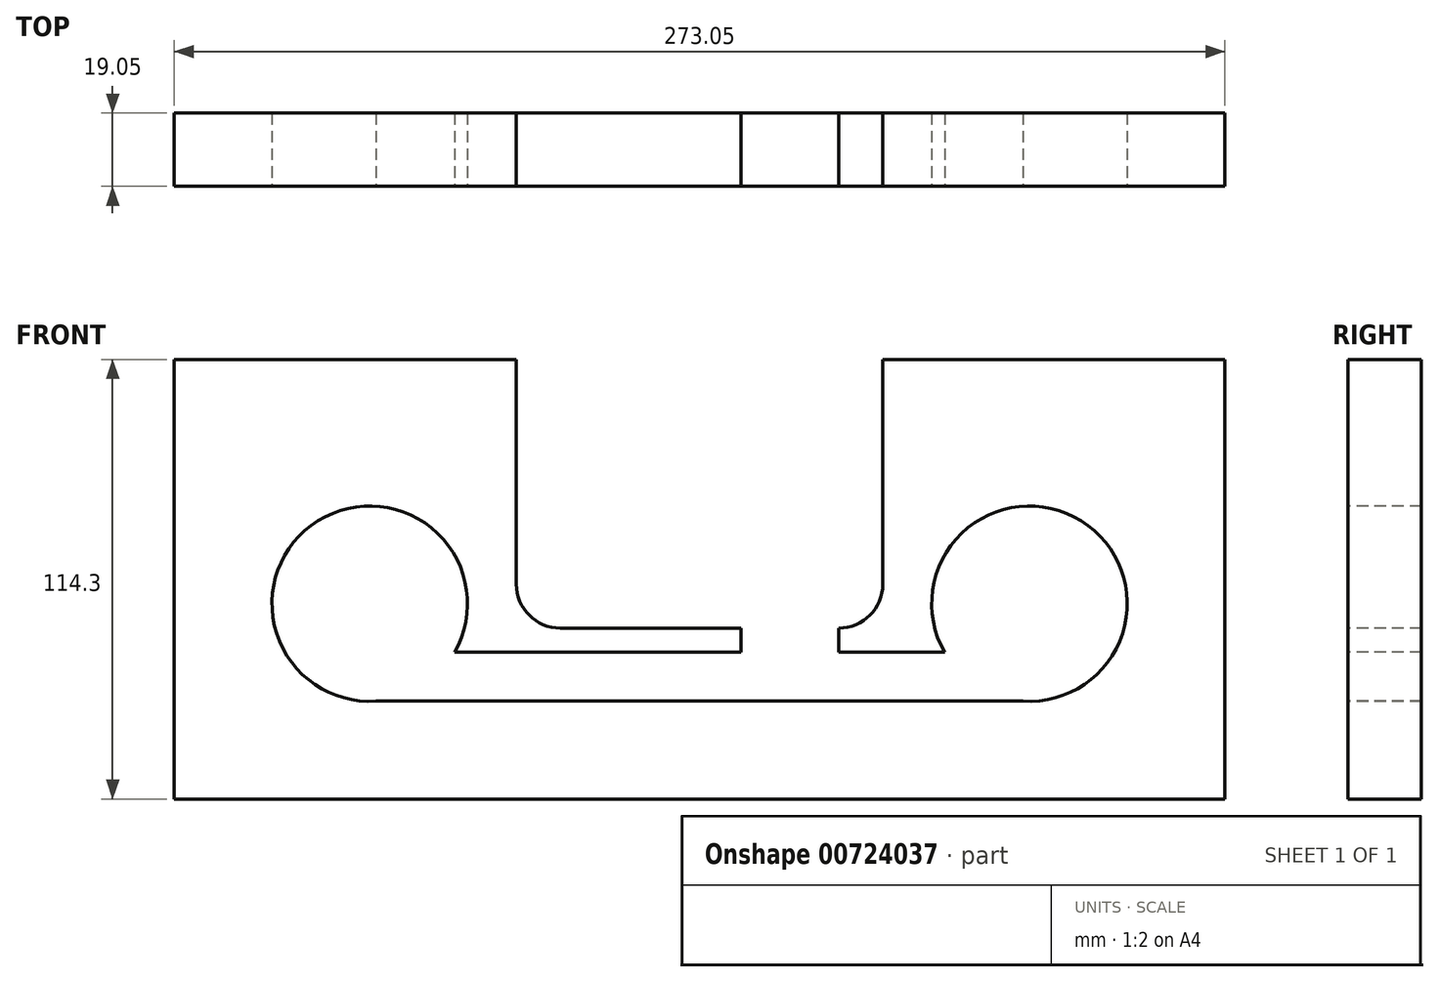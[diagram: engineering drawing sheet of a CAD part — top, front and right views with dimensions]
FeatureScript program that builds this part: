
annotation { "Feature Type Name" : "Feature", "Feature Type Description" : "" }
export const myFeature = defineFeature(function(context is Context, id is Id, definition is map)
    precondition{}
    {
        {
            var Q0;
            Q0=qCreatedBy(makeId("Front.planeOp"),FACE);
            var sketch = newSketch(context, id + "F0", { "sketchPlane" : qUnion([Q0])});
            skLineSegment(sketch, "E0.bottom", {"start": v(0, 0) * mm, "end": v(273.05, 0) * mm});
            skLineSegment(sketch, "E0.top", {"start": v(0, 114.3) * mm, "end": v(273.05, 114.3) * mm});
            skLineSegment(sketch, "E0.left", {"start": v(0, 0) * mm, "end": v(0, 114.3) * mm});
            skLineSegment(sketch, "E0.right", {"start": v(273.05, 0) * mm, "end": v(273.05, 114.3) * mm});
            skSolve(sketch);
        }
        {
            var Q0;
            Q0=qSketchRegion(id+"F0",true);
            extrude(context, id + "F1", {"entities" : qUnion([Q0]), "depth" : 19.05 * mm, "offsetDistance" : 25.4 * mm});
        }
        {
            var Q0;
            Q0=makeQuery(id+"F1.opExtrude","CAP_FACE",FACE,{"disambiguationData":[OSD([sQuery(id+"F0.wireOp",EDGE,"E0.bottom"),sQuery(id+"F0.wireOp",EDGE,"E0.top"),sQuery(id+"F0.wireOp",EDGE,"E0.left"),sQuery(id+"F0.wireOp",EDGE,"E0.right")])],"isStart":false});
            var sketch = newSketch(context, id + "F2", { "sketchPlane" : qUnion([Q0])});
            skCircle(sketch, "E1", {"center": v(50.8, 50.8) * mm, "radius": 25.4 * mm});
            skCircle(sketch, "E2", {"center": v(222.25, 50.8) * mm, "radius": 25.4 * mm});
            skLineSegment(sketch, "E3", {"start": v(88.9, 114.3) * mm, "end": v(88.9, 55.88) * mm});
            skLineSegment(sketch, "E4", {"start": v(100.33, 44.45) * mm, "end": v(172.72, 44.45) * mm});
            skLineSegment(sketch, "E5", {"start": v(184.15, 55.88) * mm, "end": v(184.15, 114.3) * mm});
            skPoint(sketch, "E6.visualSharp", {"position": v(88.9, 44.45) * mm});
            skArc(sketch, "E6.filletArc", {"start": v(88.9, 55.88) * mm, "mid": v(92.25, 47.8) * mm, "end": v(100.33, 44.45) * mm});
            skPoint(sketch, "E7.visualSharp", {"position": v(184.15, 44.45) * mm});
            skArc(sketch, "E7.filletArc", {"start": v(172.72, 44.45) * mm, "mid": v(180.8, 47.8) * mm, "end": v(184.15, 55.88) * mm});
            skLineSegment(sketch, "E8", {"start": v(151.05, 44.45) * mm, "end": v(151.05, 38.12) * mm});
            skLineSegment(sketch, "E9", {"start": v(151.05, 38.12) * mm, "end": v(64.33, 38.12) * mm});
            skLineSegment(sketch, "E10", {"start": v(64.33, 38.12) * mm, "end": v(51.78, 25.42) * mm});
            skLineSegment(sketch, "E11", {"start": v(51.78, 25.42) * mm, "end": v(223.23, 25.42) * mm});
            skLineSegment(sketch, "E12", {"start": v(223.23, 25.42) * mm, "end": v(207.7, 38.12) * mm});
            skLineSegment(sketch, "E13", {"start": v(207.7, 38.12) * mm, "end": v(176.45, 38.12) * mm});
            skLineSegment(sketch, "E14", {"start": v(176.45, 38.12) * mm, "end": v(176.45, 44.45) * mm});
            skSolve(sketch);
        }
        {
            var Q0;
            Q0 = qSketchRegion(id + "F2", true);
            var Q1;
            {var subQ5=sQuery(id+"F2.wireOp",EDGE,"E3");Q1=makeQuery(id+"F2.imprint","IMPRINT",FACE,{"disambiguationData":[TD([[makeQuery(id+"F2.imprint","IMPRINT",EDGE,{"derivedFrom":subQ5}),1.0]])]});}
            extrude(context, id + "F3", {"entities" : qUnion([Q0, Q1]), "operationType" : NewBodyOperationType.REMOVE, "oppositeDirection" : true, "depth" : 25.4 * mm, "offsetDistance" : 25.4 * mm});
        }
        {
            var Q0;
            Q0=makeQuery(id+"F1.opExtrude","CAP_FACE",FACE,{"disambiguationData":[OSD([sQuery(id+"F0.wireOp",EDGE,"E0.bottom"),sQuery(id+"F0.wireOp",EDGE,"E0.top"),sQuery(id+"F0.wireOp",EDGE,"E0.left"),sQuery(id+"F0.wireOp",EDGE,"E0.right")])],"isStart":false});
            var sketch = newSketch(context, id + "F4", { "sketchPlane" : qUnion([Q0])});
            skLineSegment(sketch, "E15", {"start": v(147.32, 44.45) * mm, "end": v(147.32, 38.15) * mm});
            skLineSegment(sketch, "E16", {"start": v(147.32, 38.15) * mm, "end": v(64.33, 38.15) * mm});
            skLineSegment(sketch, "E17", {"start": v(64.33, 38.15) * mm, "end": v(52.46, 25.45) * mm});
            skLineSegment(sketch, "E18", {"start": v(52.46, 25.45) * mm, "end": v(223.9, 25.45) * mm});
            skLineSegment(sketch, "E19", {"start": v(223.9, 25.45) * mm, "end": v(209.8, 38.15) * mm});
            skLineSegment(sketch, "E20", {"start": v(209.8, 38.15) * mm, "end": v(172.72, 38.15) * mm});
            skLineSegment(sketch, "E21", {"start": v(172.72, 38.15) * mm, "end": v(172.72, 44.45) * mm});
            skSolve(sketch);
        }
        {
            var Q0;
            Q0 = qSketchRegion(id + "F4", true);
            var Q1;
            {var subQ9=sQuery(id+"F4.wireOp",EDGE,"E15");Q1=makeQuery(id+"F4.imprint","IMPRINT",FACE,{"disambiguationData":[TD([[makeQuery(id+"F4.imprint","IMPRINT",EDGE,{"derivedFrom":subQ9}),1.0]])]});}
            extrude(context, id + "F5", {"entities" : qUnion([Q0, Q1]), "operationType" : NewBodyOperationType.REMOVE, "oppositeDirection" : true, "depth" : 25.4 * mm, "offsetDistance" : 25.4 * mm});
        }
    });
